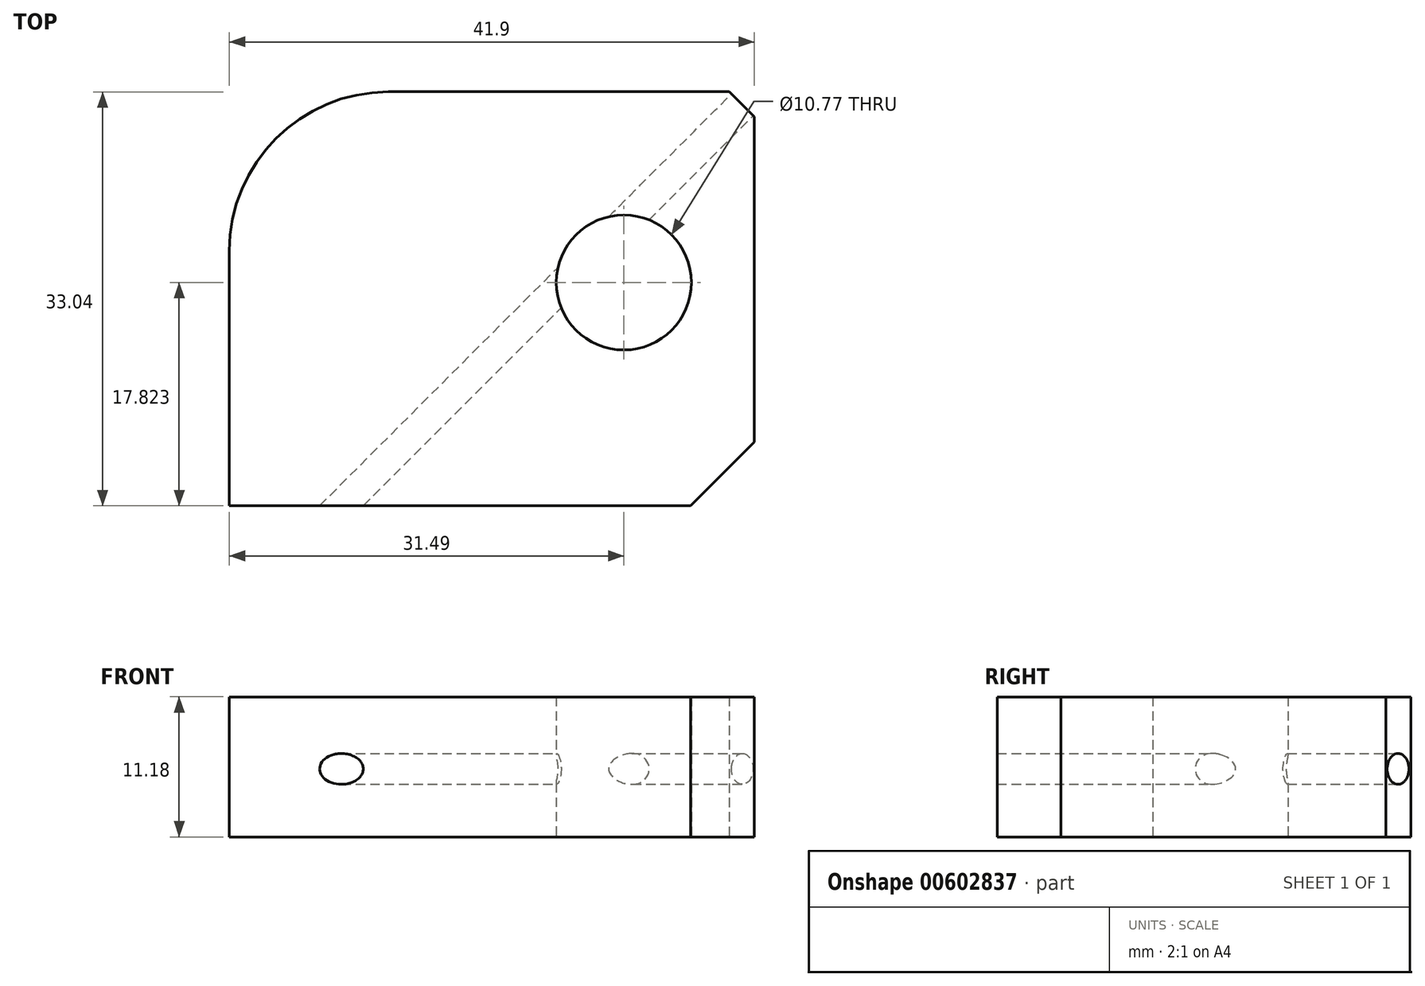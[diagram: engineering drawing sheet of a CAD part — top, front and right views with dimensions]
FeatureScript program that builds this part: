
annotation { "Feature Type Name" : "Feature", "Feature Type Description" : "" }
export const myFeature = defineFeature(function(context is Context, id is Id, definition is map)
    precondition{}
    {
        {
            var Q0;
            Q0=qCreatedBy(makeId("Top.planeOp"),FACE);
            var sketch = newSketch(context, id + "F0", { "sketchPlane" : qUnion([Q0])});
            skLineSegment(sketch, "E0.bottom", {"start": v(-23.32, -13.01) * mm, "end": v(18.58, -13.01) * mm});
            skLineSegment(sketch, "E0.top", {"start": v(-10.62, 20.03) * mm, "end": v(18.58, 20.03) * mm});
            skLineSegment(sketch, "E0.left", {"start": v(-23.32, -13.01) * mm, "end": v(-23.32, 7.33) * mm});
            skLineSegment(sketch, "E0.right", {"start": v(18.58, -13.01) * mm, "end": v(18.58, 20.03) * mm});
            skPoint(sketch, "E1.visualSharp", {"position": v(-23.32, 20.03) * mm});
            skArc(sketch, "E1.filletArc", {"start": v(-10.62, 20.03) * mm, "mid": v(-19.6, 16.31) * mm, "end": v(-23.32, 7.33) * mm});
            skCircle(sketch, "E2", {"center": v(8.17, 4.81) * mm, "radius": 5.39 * mm});
            skSolve(sketch);
        }
        {
            var Q0;
            Q0=makeQuery(id+"F0.imprint","IMPRINT",FACE,{"disambiguationData":[TD([[makeQuery(id+"F0.imprint","IMPRINT",EDGE,{"derivedFrom":sQuery(id+"F0.wireOp",EDGE,"E0.bottom")}),1.0]])]});
            extrude(context, id + "F1", {"entities" : qUnion([Q0]), "depth" : 11.18 * mm, "offsetDistance" : 25.4 * mm});
        }
        {
            var Q0;
            Q0=makeQuery(id+"F1.opExtrude","SWEPT_EDGE",EDGE,{"disambiguationData":[OSD([sQuery(id+"F0.wireOp",EDGE,"E0.bottom"),sQuery(id+"F0.wireOp",EDGE,"E0.right")])]});
            chamfer(context, id + "F2", {"entities" : qUnion([Q0]), "width" : 5.08 * mm, "tangentPropagation" : true});
        }
        {
            var Q0;
            Q0=makeQuery(id+"F1.opExtrude","SWEPT_EDGE",EDGE,{"disambiguationData":[OSD([sQuery(id+"F0.wireOp",EDGE,"E0.top"),sQuery(id+"F0.wireOp",EDGE,"E0.right")])]});
            chamfer(context, id + "F3", {"entities" : qUnion([Q0]), "width" : 2 * mm, "tangentPropagation" : true});
        }
        {
            var Q0;
            Q0=makeQuery(id+"F3.opChamfer","BLEND_FACE",FACE,{"disambiguationData":[OSD([sQuery(id+"F0.wireOp",EDGE,"E0.top"),sQuery(id+"F0.wireOp",EDGE,"E0.right")])]});
            var sketch = newSketch(context, id + "F4", { "sketchPlane" : qUnion([Q0])});
            skCircle(sketch, "E3", {"center": v(0.97, 5.43) * mm, "radius": 1.23 * mm});
            skSolve(sketch);
        }
        {
            var Q0;
            Q0=makeQuery(id+"F4.imprint","IMPRINT",FACE,{"disambiguationData":[TD([[makeQuery(id+"F4.imprint","IMPRINT",EDGE,{"derivedFrom":sQuery(id+"F4.wireOp",EDGE,"E3")}),1.0]])]});
            extrude(context, id + "F5", {"entities" : qUnion([Q0]), "operationType" : NewBodyOperationType.REMOVE, "oppositeDirection" : true, "depth" : 64.52 * mm, "offsetDistance" : 25.4 * mm});
        }
    });
